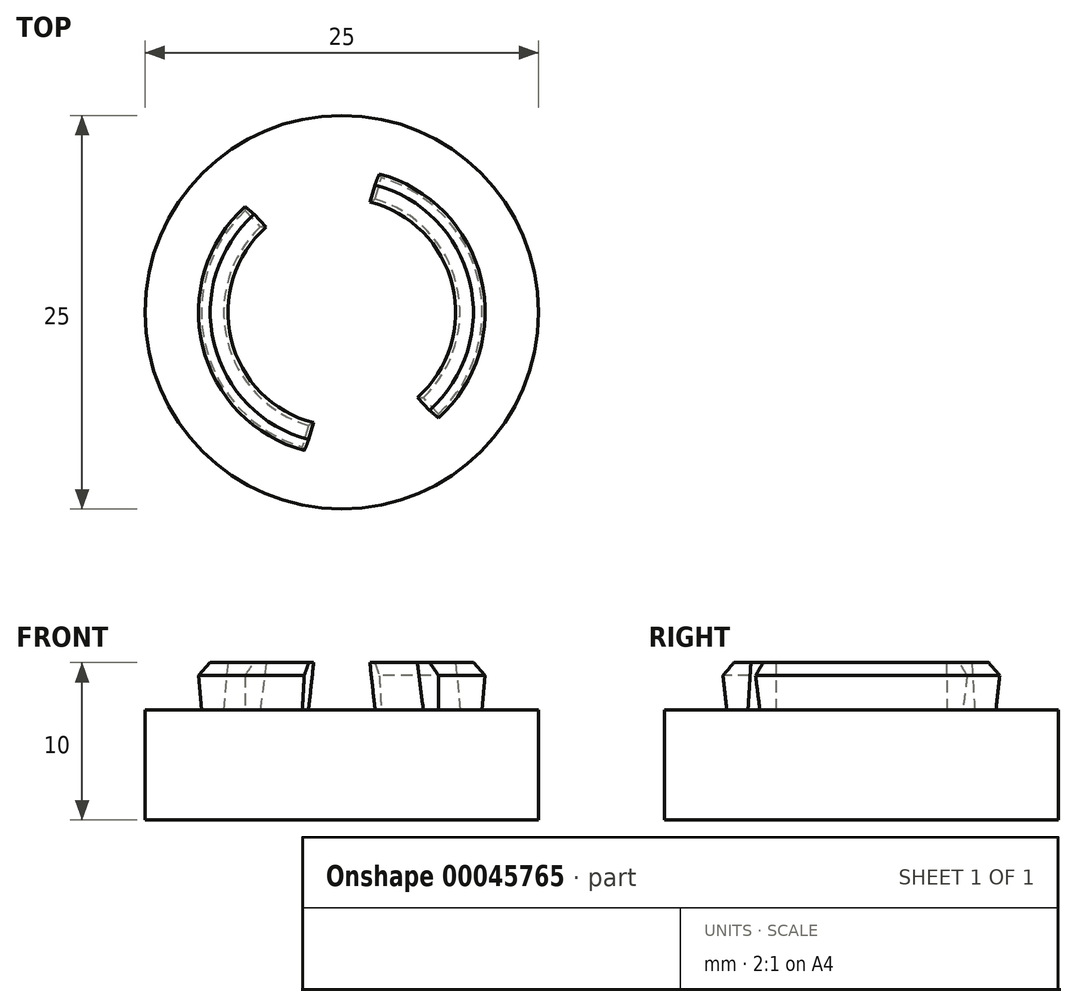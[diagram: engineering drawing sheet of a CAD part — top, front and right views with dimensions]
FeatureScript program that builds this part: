
annotation { "Feature Type Name" : "Feature", "Feature Type Description" : "" }
export const myFeature = defineFeature(function(context is Context, id is Id, definition is map)
    precondition{}
    {
        {
            var Q0;
            Q0=qCreatedBy(makeId("Top.planeOp"),FACE);
            var sketch = newSketch(context, id + "F0", { "sketchPlane" : qUnion([Q0])});
            skCircle(sketch, "E0", {"center": v(0, 0) * mm, "radius": 12.5 * mm});
            skCircle(sketch, "E1", {"center": v(0, 0) * mm, "radius": 8.6 * mm});
            skCircle(sketch, "E2", {"center": v(0, 0) * mm, "radius": 7.5 * mm});
            skSolve(sketch);
        }
        {
            var Q0;
            Q0=makeQuery(id+"F0.imprint","IMPRINT",FACE,{"disambiguationData":[TD([[makeQuery(id+"F0.imprint","IMPRINT",EDGE,{"derivedFrom":sQuery(id+"F0.wireOp",EDGE,"E0")}),1.0]])]});
            var Q1;
            Q1=makeQuery(id+"F0.imprint","IMPRINT",FACE,{"disambiguationData":[TD([[makeQuery(id+"F0.imprint","IMPRINT",EDGE,{"derivedFrom":sQuery(id+"F0.wireOp",EDGE,"E1")}),1.0]])]});
            var Q2;
            Q2=makeQuery(id+"F0.imprint","IMPRINT",FACE,{"disambiguationData":[TD([[makeQuery(id+"F0.imprint","IMPRINT",EDGE,{"derivedFrom":sQuery(id+"F0.wireOp",EDGE,"E2")}),1.0]])]});
            extrude(context, id + "F1", {"entities" : qUnion([Q0, Q1, Q2]), "oppositeDirection" : true, "depth" : 7 * mm});
        }
        {
            var Q0;
            Q0=makeQuery(id+"F1.opExtrude","CAP_FACE",FACE,{"disambiguationData":[OSD([sQuery(id+"F0.wireOp",EDGE,"E0"),sQuery(id+"F0.wireOp",EDGE,"E2")])],"isStart":true});
            var sketch = newSketch(context, id + "F2", { "sketchPlane" : qUnion([Q0])});
            skCircle(sketch, "E3.cCircle", {"center": v(0, 0) * mm, "radius": 8.91 * mm});
            skLineSegment(sketch, "E3.0", {"start": v(2.5, 8.55) * mm, "end": v(8.66, 2.1) * mm, "construction": true});
            skLineSegment(sketch, "E3.1", {"start": v(8.66, 2.1) * mm, "end": v(6.15, -6.45) * mm, "construction": true});
            skLineSegment(sketch, "E3.2", {"start": v(6.15, -6.45) * mm, "end": v(-2.5, -8.55) * mm, "construction": true});
            skLineSegment(sketch, "E3.3", {"start": v(-2.5, -8.55) * mm, "end": v(-8.66, -2.1) * mm, "construction": true});
            skLineSegment(sketch, "E3.4", {"start": v(-8.66, -2.1) * mm, "end": v(-6.15, 6.45) * mm, "construction": true});
            skLineSegment(sketch, "E3.5", {"start": v(-6.15, 6.45) * mm, "end": v(2.5, 8.55) * mm, "construction": true});
            skLineSegment(sketch, "E4", {"start": v(-6.15, 6.45) * mm, "end": v(0, 0) * mm});
            skLineSegment(sketch, "E5", {"start": v(2.5, 8.55) * mm, "end": v(0, 0) * mm});
            skLineSegment(sketch, "E6", {"start": v(8.66, 2.1) * mm, "end": v(0, 0) * mm});
            skLineSegment(sketch, "E7", {"start": v(6.15, -6.45) * mm, "end": v(0, 0) * mm});
            skLineSegment(sketch, "E8", {"start": v(-2.5, -8.55) * mm, "end": v(0, 0) * mm});
            skLineSegment(sketch, "E9", {"start": v(-8.66, -2.1) * mm, "end": v(0, 0) * mm});
            skCircle(sketch, "E10.0", {"center": v(0, 0) * mm, "radius": 7.5 * mm});
            skSolve(sketch);
        }
        {
            var Q0;
            {var subQ3=sQuery(id+"F2.wireOp",EDGE,"E8");var subQ5=sQuery(id+"F2.wireOp",EDGE,"E3.cCircle");var subQ7=makeQuery(id+"F2.imprint","INTERSECT",VERTEX,{"derivedFrom":[subQ5,subQ3]});Q0=makeQuery(id+"F2.imprint","IMPRINT",FACE,{"disambiguationData":[TD([[makeQuery(id+"F2.imprint","IMPRINT",EDGE,{"disambiguationData":[TD([[subQ7,1.0]])],"derivedFrom":subQ5}),1.0]])]});}
            var Q1;
            {var subQ3=sQuery(id+"F2.wireOp",EDGE,"E3.cCircle");var subQ5=sQuery(id+"F2.wireOp",EDGE,"E4");var subQ7=makeQuery(id+"F2.imprint","INTERSECT",VERTEX,{"derivedFrom":[subQ3,subQ5]});Q1=makeQuery(id+"F2.imprint","IMPRINT",FACE,{"disambiguationData":[TD([[makeQuery(id+"F2.imprint","IMPRINT",EDGE,{"disambiguationData":[TD([[subQ7,-1.0]])],"derivedFrom":subQ3}),1.0]])]});}
            var Q2;
            {var subQ4=sQuery(id+"F2.wireOp",EDGE,"E5");var subQ6=sQuery(id+"F2.wireOp",EDGE,"E3.cCircle");var subQ7=makeQuery(id+"F2.imprint","INTERSECT",VERTEX,{"derivedFrom":[subQ6,subQ4]});Q2=makeQuery(id+"F2.imprint","IMPRINT",FACE,{"disambiguationData":[TD([[makeQuery(id+"F2.imprint","IMPRINT",EDGE,{"disambiguationData":[TD([[subQ7,1.0]])],"derivedFrom":subQ6}),1.0]])]});}
            extrude(context, id + "F3", {"entities" : qUnion([Q0, Q1, Q2]), "operationType" : NewBodyOperationType.ADD, "depth" : 3 * mm, "hasDraft" : true, "draftAngle" : 5 * degree});
        }
        {
            var Q0;
            {var subQ0=sQuery(id+"F2.wireOp",EDGE,"E3.cCircle");Q0=makeQuery(id+"F3.opExtrude","CAP_EDGE",EDGE,{"disambiguationData":[OSD([subQ0]),TDD([makeQuery(id+"F2.imprint","IMPRINT",EDGE,{"disambiguationData":[TD([[makeQuery(id+"F2.imprint","INTERSECT",VERTEX,{"derivedFrom":[subQ0,sQuery(id+"F2.wireOp",EDGE,"E4")]}),-1.0]])],"derivedFrom":subQ0}),makeQuery(id+"F2.imprint","IMPRINT",EDGE,{"disambiguationData":[TD([[makeQuery(id+"F2.imprint","INTERSECT",VERTEX,{"derivedFrom":[subQ0,sQuery(id+"F2.wireOp",EDGE,"E8")]}),1.0]])],"derivedFrom":subQ0})])],"isStart":false});}
            var Q1;
            {var subQ0=sQuery(id+"F2.wireOp",EDGE,"E3.cCircle");Q1=makeQuery(id+"F3.opExtrude","CAP_EDGE",EDGE,{"disambiguationData":[OSD([subQ0]),TDD([makeQuery(id+"F2.imprint","IMPRINT",EDGE,{"disambiguationData":[TD([[makeQuery(id+"F2.imprint","INTERSECT",VERTEX,{"derivedFrom":[subQ0,sQuery(id+"F2.wireOp",EDGE,"E5")]}),1.0]])],"derivedFrom":subQ0})])],"isStart":false});}
            chamfer(context, id + "F4", {"entities" : qUnion([Q0, Q1]), "width" : .75 * mm, "tangentPropagation" : true});
        }
    });
